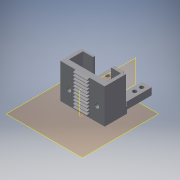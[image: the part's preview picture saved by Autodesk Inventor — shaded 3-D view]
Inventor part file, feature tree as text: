
AUTODESK INVENTOR PART (.ipt)
format: ipt  version: 2019.4 (Build 234330000, 330)  size: 370,688 bytes
history: native  units: mm
features: reference x19, extrude x11, sketch x11, other x11, projected_geometry x4, plane x2, mirror x1, hole x1, fillet x1, pattern_linear x1
ambient origin geometry x8: Origin, YZ Plane, XZ Plane, XY Plane, X Axis, Y Axis, Z Axis, Center Point
bodies: Body1 (feature_tree)
feature tree (62):
  plane  "Work Plane8"
  extrude  "Extrusion11"  Depth=5.0mm TaperAngle=0.0deg
  extrude  "Extrusion12"  TaperAngle=45.0deg  [1 undecoded]
  extrude  "Extrusion15"  Depth=4.5mm TaperAngle=0.0deg
  mirror  "Mirror3"
  extrude  "Extrusion16"  Depth=20.0mm TaperAngle=0.0deg
  extrude  "Extrusion17"  TaperAngle=0.0deg  [1 undecoded]
  hole  "Hole1"  [1 undecoded]
  extrude  "Extrusion18"  Depth=10.0mm TaperAngle=0.0deg
  extrude  "Extrusion19"  Depth=10.0mm TaperAngle=0.0deg
  extrude  "Extrusion20"  Depth=2.0mm
  extrude  "Extrusion21"  Depth=0.4mm
  plane  "Work Plane9"
  extrude  "Extrusion22"  Depth=10.0mm TaperAngle=0.0deg
  fillet  "Fillet1"  Radius=0.3mm
  pattern_linear  "Rectangular Pattern2"  Count1=11 Spacing1=2.186mm
  extrude  "Extrusion23"  TaperAngle=0.0deg  [1 undecoded]
  sketch  "Sketch12"  dims[d64=180.0deg d66=5.0mm d67=0.0mm]
  reference  "Reference31"
  reference  "Reference32"
  reference  "Reference33"
  reference  "Reference35"
  reference  "Reference36"
  sketch  "Sketch16"  dims[d70=10.0mm d71=0.0mm d80=45.0deg]
  projected_geometry  "Projected Loop9"
  reference  "Reference41"
  reference  "Reference42"
  sketch  "Sketch17"  dims[d81=8.0mm d82=0.0mm d83=4.5mm d84=0.0mm]
  reference  "Reference44"
  reference  "Reference45"
  reference  "Reference46"
  reference  "Reference47"
  sketch  "Sketch18"  dims[d85=4.0mm d86=20.0mm d87=0.0mm]
  projected_geometry  "Projected Loop10"
  sketch  "Sketch19"  dims[d89=3.2mm d90=6.0mm d91=6.0mm d92=22.0mm d93=90.0deg d94=8.0mm d95=20.594885mm d96=0.0mm]
  reference  "Reference48"
  reference  "Reference49"
  sketch  "Sketch20"  dims[d97=10.0mm d98=0.0mm d99=0.5mm]
  reference  "Reference50"
  reference  "Reference51"
  reference  "Reference52"
  reference  "Reference53"
  sketch  "Sketch21"  dims[d100=0.5mm d101=10.0mm d102=0.0mm]
  reference  "Reference54"
  sketch  "Sketch22"  dims[d103=6.0mm d104=10.0mm d105=0.0mm]
  reference  "Reference55"
  sketch  "Sketch23"  dims[d106=0.0mm d107=0.0mm d108=2.0mm]
  sketch  "Sketch24"  dims[d109=27.925268mm d1=0.4mm]
  projected_geometry  "Projected Loop11"
  sketch  "Sketch25"  dims[d111=19.198622mm d114=10.0mm d115=0.0mm d119=0.3mm d120=110.0mm d122=2.186mm d123=0.0mm d124=0.0mm]
  projected_geometry  "Projected Loop12"
  other  "Assembly_Cube_Z_Focus_Drylin_NEMA_v3.iam"
  other  "00_Igus_Drylin_6mm:1"
  other  "00_Igus_Drylin_6mm:4"
  other  "30_Cube_Z_Focus_MGN_NEMA_adapter:1"
  other  "30_Cube_Z_Focus_Drylin_NEMA_base_v3:1"
  other  "Assembly_Cube_Z_Focus_Drylin_NEMA_slide.iam"
  other  "30_Cube_Z_Focus_Drylin_NEMA_slide_part1:1"
  other  "30_Cube_Z_Focus_Drylin_NEMA_slide_part2:1"
  other  "Assembly_Cube_Z_Focus_MGN_NEMA_v3.iam"
  other  "00_MGN12H, LINEAR GUIDE BLOCK:1"
  other  "DIN 912 - replaced by DIN EN ISO 4762 M3 x 30:1"
note: 4 required parameter values undecoded (feature->parameter linkage not recoverable at this tier; creation-order binding heuristic only, values carry confidence <= 0.55)
